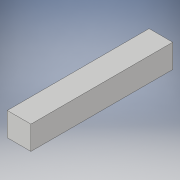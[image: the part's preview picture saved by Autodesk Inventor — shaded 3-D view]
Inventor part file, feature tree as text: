
AUTODESK INVENTOR PART (.ipt)
format: ipt  version: 2018 (Build 220112000, 112)  size: 92,672 bytes
history: native  units: in
note: dims shown in document units (in); Inventor stores cm internally (conversion verified against a paired STEP export)
features: extrude x1, sketch x1
ambient origin geometry x8: Origin, YZ Plane, XZ Plane, XY Plane, X Axis, Y Axis, Z Axis, Center Point
bodies: Solid1 (feature_tree)
feature tree (2):
  extrude  "Extrusion1"  Depth=6.0in
  sketch  "Sketch1"  dims[d0=1.0in d1=6.0in d2=1.0in d3=0.0in]
